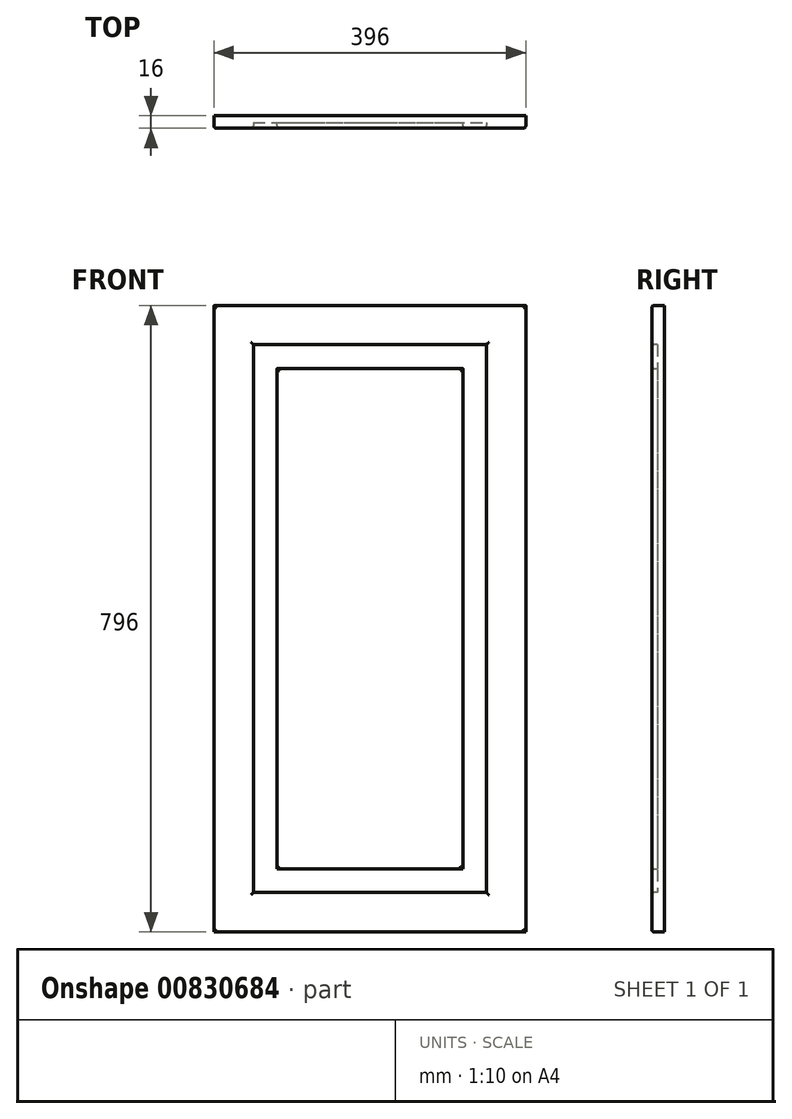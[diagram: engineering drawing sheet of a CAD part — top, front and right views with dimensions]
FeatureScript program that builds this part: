
annotation { "Feature Type Name" : "Feature", "Feature Type Description" : "" }
export const myFeature = defineFeature(function(context is Context, id is Id, definition is map)
    precondition{}
    {
        {
            var Q0;
            Q0=qCreatedBy(makeId("Front.planeOp"),FACE);
            var sketch = newSketch(context, id + "F0", { "sketchPlane" : qUnion([Q0])});
            skLineSegment(sketch, "E0.bottom", {"start": v(0, 0) * mm, "end": v(44.66, 0) * mm});
            skLineSegment(sketch, "E0.top", {"start": v(0, 33.8) * mm, "end": v(44.66, 33.8) * mm});
            skLineSegment(sketch, "E0.left", {"start": v(0, 0) * mm, "end": v(0, 33.8) * mm});
            skLineSegment(sketch, "E0.right", {"start": v(44.66, 0) * mm, "end": v(44.66, 33.8) * mm});
            skSolve(sketch);
        }
        {
            var Q0;
            Q0=makeQuery(id+"F0.imprint","IMPRINT",FACE,{"disambiguationData":[TD([[makeQuery(id+"F0.imprint","IMPRINT",EDGE,{"derivedFrom":sQuery(id+"F0.wireOp",EDGE,"E0.bottom")}),1.0]])]});
            extrude(context, id + "F1", {"entities" : qUnion([Q0]), "depth" : 16 * mm, "offsetDistance" : 25.4 * mm});
        }
        {
            var Q0;
            Q0=makeQuery(id+"F1.opExtrude","SWEPT_FACE",FACE,{"disambiguationData":[OSD([sQuery(id+"F0.wireOp",EDGE,"E0.bottom")])]});
            extrude(context, id + "F2", {"entities" : qUnion([Q0]), "operationType" : NewBodyOperationType.ADD, "oppositeDirection" : true, "depth" : 796 * mm, "offsetDistance" : 25 * mm});
        }
        {
            var Q0;
            {var subQ0=sQuery(id+"F0.wireOp",EDGE,"E0.left");Q0=makeQuery(id+"F2.boolean.opBoolean","MERGE",FACE,{"derivedFrom":[makeQuery(id+"F1.opExtrude","SWEPT_FACE",FACE,{"disambiguationData":[OSD([subQ0])]}),makeQuery(id+"F2.opExtrude","SWEPT_FACE",FACE,{"disambiguationData":[OSD([sQuery(id+"F0.wireOp",EDGE,"E0.bottom"),subQ0])]})]});}
            extrude(context, id + "F3", {"entities" : qUnion([Q0]), "operationType" : NewBodyOperationType.ADD, "oppositeDirection" : true, "depth" : 196 * mm, "offsetDistance" : 25 * mm});
        }
        {
            var Q0;
            {var subQ0=sQuery(id+"F0.wireOp",EDGE,"E0.left");var subQ1=sQuery(id+"F0.wireOp",EDGE,"E0.bottom");Q0=makeQuery(id+"F3.boolean.opBoolean","MERGE",FACE,{"derivedFrom":[makeQuery(id+"F2.boolean.opBoolean","MERGE",FACE,{"derivedFrom":[makeQuery(id+"F1.opExtrude","CAP_FACE",FACE,{"disambiguationData":[OSD([subQ1,sQuery(id+"F0.wireOp",EDGE,"E0.top"),subQ0,sQuery(id+"F0.wireOp",EDGE,"E0.right")])],"isStart":false}),makeQuery(id+"F2.opExtrude","SWEPT_FACE",FACE,{"disambiguationData":[OSD([subQ1]),TDD([makeQuery(id+"F1.opExtrude","CAP_EDGE",EDGE,{"disambiguationData":[OSD([subQ1])],"isStart":false})])]})]}),makeQuery(id+"F3.opExtrude","SWEPT_FACE",FACE,{"disambiguationData":[OSD([subQ1,subQ0]),TDD([makeQuery(id+"F2.boolean.opBoolean","MERGE",EDGE,{"derivedFrom":[makeQuery(id+"F1.opExtrude","CAP_EDGE",EDGE,{"disambiguationData":[OSD([subQ0])],"isStart":false}),makeQuery(id+"F2.opExtrude","SWEPT_EDGE",EDGE,{"disambiguationData":[OSD([subQ1,subQ0]),TDD([makeQuery(id+"F1.opExtrude","CAP_VERTEX",VERTEX,{"disambiguationData":[OSD([subQ1,subQ0])],"isStart":false})])]})]})])]})]});}
            var sketch = newSketch(context, id + "F4", { "sketchPlane" : qUnion([Q0])});
            skLineSegment(sketch, "E1.bottom", {"start": v(59.7, 646.67) * mm, "end": v(128.66, 646.67) * mm});
            skLineSegment(sketch, "E1.top", {"start": v(59.7, 152.97) * mm, "end": v(128.66, 152.97) * mm});
            skLineSegment(sketch, "E1.left", {"start": v(59.7, 646.67) * mm, "end": v(59.7, 152.97) * mm});
            skLineSegment(sketch, "E1.right", {"start": v(128.66, 646.67) * mm, "end": v(128.66, 152.97) * mm});
            skSolve(sketch);
        }
        {
            var Q0;
            Q0=makeQuery(id+"F4.imprint","IMPRINT",FACE,{"disambiguationData":[TD([[makeQuery(id+"F4.imprint","IMPRINT",EDGE,{"derivedFrom":sQuery(id+"F4.wireOp",EDGE,"E1.bottom")}),-1.0]])]});
            extrude(context, id + "F5", {"entities" : qUnion([Q0]), "operationType" : NewBodyOperationType.REMOVE, "oppositeDirection" : true, "depth" : 7 * mm, "offsetDistance" : 25 * mm});
        }
        {
            var Q0;
            Q0=makeQuery(id+"F5.boolean.opBoolean","COPY",FACE,{"derivedFrom":makeQuery(id+"F5.opExtrude","SWEPT_FACE",FACE,{"disambiguationData":[OSD([sQuery(id+"F4.wireOp",EDGE,"E1.left")])]})});
            extrude(context, id + "F6", {"entities" : qUnion([Q0]), "operationType" : NewBodyOperationType.REMOVE, "oppositeDirection" : true, "depth" : 9.7 * mm, "offsetDistance" : 25 * mm});
        }
        {
            var Q0;
            {var subQ0=sQuery(id+"F4.wireOp",EDGE,"E1.bottom");Q0=makeQuery(id+"F6.boolean.opBoolean","MERGE",FACE,{"derivedFrom":[makeQuery(id+"F5.boolean.opBoolean","COPY",FACE,{"derivedFrom":makeQuery(id+"F5.opExtrude","SWEPT_FACE",FACE,{"disambiguationData":[OSD([subQ0])]})}),makeQuery(id+"F6.opExtrude","SWEPT_FACE",FACE,{"disambiguationData":[OSD([subQ0,sQuery(id+"F4.wireOp",EDGE,"E1.left")])]})]});}
            extrude(context, id + "F7", {"entities" : qUnion([Q0]), "operationType" : NewBodyOperationType.ADD, "oppositeDirection" : true, "depth" : 99.33 * mm, "offsetDistance" : 25 * mm});
        }
        {
            var Q0;
            {var subQ0=sQuery(id+"F4.wireOp",EDGE,"E1.bottom");Q0=makeQuery(id+"F6.boolean.opBoolean","MERGE",FACE,{"derivedFrom":[makeQuery(id+"F5.boolean.opBoolean","COPY",FACE,{"derivedFrom":makeQuery(id+"F5.opExtrude","SWEPT_FACE",FACE,{"disambiguationData":[OSD([subQ0])]})}),makeQuery(id+"F6.opExtrude","SWEPT_FACE",FACE,{"disambiguationData":[OSD([subQ0,sQuery(id+"F4.wireOp",EDGE,"E1.left")])]})]});}
            extrude(context, id + "F8", {"entities" : qUnion([Q0]), "operationType" : NewBodyOperationType.REMOVE, "oppositeDirection" : true, "depth" : 99.33 * mm, "offsetDistance" : 25 * mm});
        }
        {
            var Q0;
            {var subQ0=sQuery(id+"F4.wireOp",EDGE,"E1.right");Q0=makeQuery(id+"F8.boolean.opBoolean","MERGE",FACE,{"derivedFrom":[makeQuery(id+"F5.boolean.opBoolean","COPY",FACE,{"derivedFrom":makeQuery(id+"F5.opExtrude","SWEPT_FACE",FACE,{"disambiguationData":[OSD([subQ0])]})}),makeQuery(id+"F8.opExtrude","SWEPT_FACE",FACE,{"disambiguationData":[OSD([sQuery(id+"F4.wireOp",EDGE,"E1.bottom"),subQ0])]})]});}
            extrude(context, id + "F9", {"entities" : qUnion([Q0]), "operationType" : NewBodyOperationType.REMOVE, "oppositeDirection" : true, "depth" : 17.34 * mm, "offsetDistance" : 25 * mm});
        }
        {
            var Q0;
            {var subQ0=sQuery(id+"F4.wireOp",EDGE,"E1.top");Q0=makeQuery(id+"F9.boolean.opBoolean","MERGE",FACE,{"derivedFrom":[makeQuery(id+"F6.boolean.opBoolean","MERGE",FACE,{"derivedFrom":[makeQuery(id+"F5.boolean.opBoolean","COPY",FACE,{"derivedFrom":makeQuery(id+"F5.opExtrude","SWEPT_FACE",FACE,{"disambiguationData":[OSD([subQ0])]})}),makeQuery(id+"F6.opExtrude","SWEPT_FACE",FACE,{"disambiguationData":[OSD([subQ0,sQuery(id+"F4.wireOp",EDGE,"E1.left")])]})]}),makeQuery(id+"F9.opExtrude","SWEPT_FACE",FACE,{"disambiguationData":[OSD([subQ0,sQuery(id+"F4.wireOp",EDGE,"E1.right")])]})]});}
            extrude(context, id + "F10", {"entities" : qUnion([Q0]), "operationType" : NewBodyOperationType.REMOVE, "oppositeDirection" : true, "depth" : 102.97 * mm, "offsetDistance" : 25 * mm});
        }
        {
            var Q0;
            {var subQ0=sQuery(id+"F4.wireOp",EDGE,"E1.right");var subQ1=sQuery(id+"F4.wireOp",EDGE,"E1.top");var subQ2=sQuery(id+"F4.wireOp",EDGE,"E1.left");var subQ3=sQuery(id+"F4.wireOp",EDGE,"E1.bottom");Q0=makeQuery(id+"F10.boolean.opBoolean","MERGE",FACE,{"derivedFrom":[makeQuery(id+"F9.boolean.opBoolean","MERGE",FACE,{"derivedFrom":[makeQuery(id+"F8.boolean.opBoolean","MERGE",FACE,{"derivedFrom":[makeQuery(id+"F6.boolean.opBoolean","MERGE",FACE,{"derivedFrom":[makeQuery(id+"F5.boolean.opBoolean","COPY",FACE,{"derivedFrom":makeQuery(id+"F5.opExtrude","CAP_FACE",FACE,{"disambiguationData":[OSD([subQ3,subQ1,subQ2,subQ0])],"isStart":false})}),makeQuery(id+"F6.opExtrude","SWEPT_FACE",FACE,{"disambiguationData":[OSD([subQ2]),TDD([makeQuery(id+"F5.boolean.opBoolean","COPY",EDGE,{"derivedFrom":makeQuery(id+"F5.opExtrude","CAP_EDGE",EDGE,{"disambiguationData":[OSD([subQ2])],"isStart":false})})])]})]}),makeQuery(id+"F8.opExtrude","SWEPT_FACE",FACE,{"disambiguationData":[OSD([subQ3,subQ2]),TDD([makeQuery(id+"F6.boolean.opBoolean","MERGE",EDGE,{"derivedFrom":[makeQuery(id+"F5.boolean.opBoolean","COPY",EDGE,{"derivedFrom":makeQuery(id+"F5.opExtrude","CAP_EDGE",EDGE,{"disambiguationData":[OSD([subQ3])],"isStart":false})}),makeQuery(id+"F6.opExtrude","SWEPT_EDGE",EDGE,{"disambiguationData":[OSD([subQ3,subQ2]),TDD([makeQuery(id+"F5.boolean.opBoolean","COPY",VERTEX,{"derivedFrom":makeQuery(id+"F5.opExtrude","CAP_VERTEX",VERTEX,{"disambiguationData":[OSD([subQ3,subQ2])],"isStart":false})})])]})]})])]})]}),makeQuery(id+"F9.opExtrude","SWEPT_FACE",FACE,{"disambiguationData":[OSD([subQ3,subQ0]),TDD([makeQuery(id+"F8.boolean.opBoolean","MERGE",EDGE,{"derivedFrom":[makeQuery(id+"F5.boolean.opBoolean","COPY",EDGE,{"derivedFrom":makeQuery(id+"F5.opExtrude","CAP_EDGE",EDGE,{"disambiguationData":[OSD([subQ0])],"isStart":false})}),makeQuery(id+"F8.opExtrude","SWEPT_EDGE",EDGE,{"disambiguationData":[OSD([subQ3,subQ0]),TDD([makeQuery(id+"F5.boolean.opBoolean","COPY",VERTEX,{"derivedFrom":makeQuery(id+"F5.opExtrude","CAP_VERTEX",VERTEX,{"disambiguationData":[OSD([subQ3,subQ0])],"isStart":false})})])]})]})])]})]}),makeQuery(id+"F10.opExtrude","SWEPT_FACE",FACE,{"disambiguationData":[OSD([subQ1,subQ2,subQ0]),TDD([makeQuery(id+"F9.boolean.opBoolean","MERGE",EDGE,{"derivedFrom":[makeQuery(id+"F6.boolean.opBoolean","MERGE",EDGE,{"derivedFrom":[makeQuery(id+"F5.boolean.opBoolean","COPY",EDGE,{"derivedFrom":makeQuery(id+"F5.opExtrude","CAP_EDGE",EDGE,{"disambiguationData":[OSD([subQ1])],"isStart":false})}),makeQuery(id+"F6.opExtrude","SWEPT_EDGE",EDGE,{"disambiguationData":[OSD([subQ1,subQ2]),TDD([makeQuery(id+"F5.boolean.opBoolean","COPY",VERTEX,{"derivedFrom":makeQuery(id+"F5.opExtrude","CAP_VERTEX",VERTEX,{"disambiguationData":[OSD([subQ1,subQ2])],"isStart":false})})])]})]}),makeQuery(id+"F9.opExtrude","SWEPT_EDGE",EDGE,{"disambiguationData":[OSD([subQ1,subQ0]),TDD([makeQuery(id+"F5.boolean.opBoolean","COPY",VERTEX,{"derivedFrom":makeQuery(id+"F5.opExtrude","CAP_VERTEX",VERTEX,{"disambiguationData":[OSD([subQ1,subQ0])],"isStart":false})})])]})]})])]})]});}
            var sketch = newSketch(context, id + "F11", { "sketchPlane" : qUnion([Q0])});
            skLineSegment(sketch, "E2.bottom", {"start": v(74.13, 678.73) * mm, "end": v(109.41, 678.73) * mm});
            skLineSegment(sketch, "E2.top", {"start": v(74.13, 186.63) * mm, "end": v(109.41, 186.63) * mm});
            skLineSegment(sketch, "E2.left", {"start": v(74.13, 678.73) * mm, "end": v(74.13, 186.63) * mm});
            skLineSegment(sketch, "E2.right", {"start": v(109.41, 678.73) * mm, "end": v(109.41, 186.63) * mm});
            skSolve(sketch);
        }
        {
            var Q0;
            Q0=makeQuery(id+"F11.imprint","IMPRINT",FACE,{"disambiguationData":[TD([[makeQuery(id+"F11.imprint","IMPRINT",EDGE,{"derivedFrom":sQuery(id+"F11.wireOp",EDGE,"E2.bottom")}),-1.0]])]});
            extrude(context, id + "F12", {"entities" : qUnion([Q0]), "operationType" : NewBodyOperationType.ADD, "depth" : 7 * mm, "offsetDistance" : 25 * mm});
        }
        {
            var Q0;
            Q0=makeQuery(id+"F12.opExtrude","SWEPT_FACE",FACE,{"disambiguationData":[OSD([sQuery(id+"F11.wireOp",EDGE,"E2.bottom")])]});
            extrude(context, id + "F13", {"entities" : qUnion([Q0]), "operationType" : NewBodyOperationType.ADD, "depth" : 37.27 * mm, "offsetDistance" : 25 * mm});
        }
        {
            var Q0;
            {var subQ0=sQuery(id+"F11.wireOp",EDGE,"E2.right");Q0=makeQuery(id+"F13.boolean.opBoolean","MERGE",FACE,{"derivedFrom":[makeQuery(id+"F12.opExtrude","SWEPT_FACE",FACE,{"disambiguationData":[OSD([subQ0])]}),makeQuery(id+"F13.opExtrude","SWEPT_FACE",FACE,{"disambiguationData":[OSD([sQuery(id+"F11.wireOp",EDGE,"E2.bottom"),subQ0])]})]});}
            extrude(context, id + "F14", {"entities" : qUnion([Q0]), "operationType" : NewBodyOperationType.ADD, "depth" : 6.58 * mm, "offsetDistance" : 25 * mm});
        }
        {
            var Q0;
            {var subQ0=sQuery(id+"F11.wireOp",EDGE,"E2.top");Q0=makeQuery(id+"F14.boolean.opBoolean","MERGE",FACE,{"derivedFrom":[makeQuery(id+"F12.opExtrude","SWEPT_FACE",FACE,{"disambiguationData":[OSD([subQ0])]}),makeQuery(id+"F14.opExtrude","SWEPT_FACE",FACE,{"disambiguationData":[OSD([subQ0,sQuery(id+"F11.wireOp",EDGE,"E2.right")])]})]});}
            extrude(context, id + "F15", {"entities" : qUnion([Q0]), "operationType" : NewBodyOperationType.ADD, "depth" : 106.63 * mm, "offsetDistance" : 25 * mm});
        }
        {
            var Q0;
            {var subQ0=sQuery(id+"F11.wireOp",EDGE,"E2.left");Q0=makeQuery(id+"F15.boolean.opBoolean","MERGE",FACE,{"derivedFrom":[makeQuery(id+"F13.boolean.opBoolean","MERGE",FACE,{"derivedFrom":[makeQuery(id+"F12.opExtrude","SWEPT_FACE",FACE,{"disambiguationData":[OSD([subQ0])]}),makeQuery(id+"F13.opExtrude","SWEPT_FACE",FACE,{"disambiguationData":[OSD([sQuery(id+"F11.wireOp",EDGE,"E2.bottom"),subQ0])]})]}),makeQuery(id+"F15.opExtrude","SWEPT_FACE",FACE,{"disambiguationData":[OSD([sQuery(id+"F11.wireOp",EDGE,"E2.top"),subQ0])]})]});}
            extrude(context, id + "F16", {"entities" : qUnion([Q0]), "operationType" : NewBodyOperationType.REMOVE, "oppositeDirection" : true, "depth" : 5.87 * mm, "offsetDistance" : 25 * mm});
        }
        {
            var Q0;
            Q0=makeQuery(id+"F3.opExtrude","CAP_FACE",FACE,{"disambiguationData":[OSD([sQuery(id+"F0.wireOp",EDGE,"E0.bottom"),sQuery(id+"F0.wireOp",EDGE,"E0.left")])],"isStart":false});
            extrude(context, id + "F17", {"entities" : qUnion([Q0]), "operationType" : NewBodyOperationType.ADD, "depth" : 200 * mm, "offsetDistance" : 25 * mm});
        }
        {
            var Q0;
            {var subQ0=sQuery(id+"F4.wireOp",EDGE,"E1.right");Q0=makeQuery(id+"F10.boolean.opBoolean","MERGE",FACE,{"derivedFrom":[makeQuery(id+"F9.boolean.opBoolean","COPY",FACE,{"derivedFrom":makeQuery(id+"F9.opExtrude","CAP_FACE",FACE,{"disambiguationData":[OSD([sQuery(id+"F4.wireOp",EDGE,"E1.bottom"),subQ0])],"isStart":false})}),makeQuery(id+"F10.opExtrude","SWEPT_FACE",FACE,{"disambiguationData":[OSD([sQuery(id+"F4.wireOp",EDGE,"E1.top"),subQ0])]})]});}
            extrude(context, id + "F18", {"entities" : qUnion([Q0]), "operationType" : NewBodyOperationType.REMOVE, "oppositeDirection" : true, "depth" : 200 * mm, "offsetDistance" : 25 * mm});
        }
        {
            var Q0;
            {var subQ0=sQuery(id+"F11.wireOp",EDGE,"E2.right");var subQ1=sQuery(id+"F11.wireOp",EDGE,"E2.top");Q0=makeQuery(id+"F15.boolean.opBoolean","MERGE",FACE,{"derivedFrom":[makeQuery(id+"F14.opExtrude","CAP_FACE",FACE,{"disambiguationData":[OSD([sQuery(id+"F11.wireOp",EDGE,"E2.bottom"),subQ0])],"isStart":false}),makeQuery(id+"F15.opExtrude","SWEPT_FACE",FACE,{"disambiguationData":[OSD([subQ1,subQ0]),TDD([makeQuery(id+"F14.opExtrude","CAP_EDGE",EDGE,{"disambiguationData":[OSD([subQ1,subQ0])],"isStart":false})])]})]});}
            extrude(context, id + "F19", {"entities" : qUnion([Q0]), "operationType" : NewBodyOperationType.ADD, "depth" : 200 * mm, "offsetDistance" : 25 * mm});
        }
        {
            var Q0;
            {var subQ0=sQuery(id+"F11.wireOp",EDGE,"E2.right");var subQ1=sQuery(id+"F11.wireOp",EDGE,"E2.top");var subQ2=makeQuery(id+"F12.opExtrude","CAP_VERTEX",VERTEX,{"disambiguationData":[OSD([subQ1,subQ0])],"isStart":false});var subQ3=sQuery(id+"F11.wireOp",EDGE,"E2.bottom");var subQ4=makeQuery(id+"F13.boolean.opBoolean","MERGE",EDGE,{"derivedFrom":[makeQuery(id+"F12.opExtrude","CAP_EDGE",EDGE,{"disambiguationData":[OSD([subQ0])],"isStart":false}),makeQuery(id+"F13.opExtrude","SWEPT_EDGE",EDGE,{"disambiguationData":[OSD([subQ3,subQ0]),TDD([makeQuery(id+"F12.opExtrude","CAP_VERTEX",VERTEX,{"disambiguationData":[OSD([subQ3,subQ0])],"isStart":false})])]})]});Q0=makeQuery(id+"F19.boolean.opBoolean","MERGE",FACE,{"derivedFrom":[makeQuery(id+"F15.boolean.opBoolean","MERGE",FACE,{"derivedFrom":[makeQuery(id+"F14.boolean.opBoolean","MERGE",FACE,{"derivedFrom":[makeQuery(id+"F13.boolean.opBoolean","MERGE",FACE,{"derivedFrom":[makeQuery(id+"F12.opExtrude","CAP_FACE",FACE,{"disambiguationData":[OSD([subQ3,subQ1,sQuery(id+"F11.wireOp",EDGE,"E2.left"),subQ0])],"isStart":false}),makeQuery(id+"F13.opExtrude","SWEPT_FACE",FACE,{"disambiguationData":[OSD([subQ3]),TDD([makeQuery(id+"F12.opExtrude","CAP_EDGE",EDGE,{"disambiguationData":[OSD([subQ3])],"isStart":false})])]})]}),makeQuery(id+"F14.opExtrude","SWEPT_FACE",FACE,{"disambiguationData":[OSD([subQ3,subQ0]),TDD([subQ4])]})]}),makeQuery(id+"F15.opExtrude","SWEPT_FACE",FACE,{"disambiguationData":[OSD([subQ1,subQ0]),TDD([makeQuery(id+"F14.boolean.opBoolean","MERGE",EDGE,{"derivedFrom":[makeQuery(id+"F12.opExtrude","CAP_EDGE",EDGE,{"disambiguationData":[OSD([subQ1])],"isStart":false}),makeQuery(id+"F14.opExtrude","SWEPT_EDGE",EDGE,{"disambiguationData":[OSD([subQ1,subQ0]),TDD([subQ2])]})]})])]})]}),makeQuery(id+"F19.opExtrude","SWEPT_FACE",FACE,{"disambiguationData":[OSD([subQ3,subQ1,subQ0]),TDD([makeQuery(id+"F15.boolean.opBoolean","MERGE",EDGE,{"derivedFrom":[makeQuery(id+"F14.opExtrude","CAP_EDGE",EDGE,{"disambiguationData":[OSD([subQ3,subQ0]),TDD([subQ4])],"isStart":false}),makeQuery(id+"F15.opExtrude","SWEPT_EDGE",EDGE,{"disambiguationData":[OSD([subQ1,subQ0]),TDD([makeQuery(id+"F14.opExtrude","CAP_VERTEX",VERTEX,{"disambiguationData":[OSD([subQ1,subQ0]),TDD([subQ2])],"isStart":false})])]})]})])]})]});}
            var Q1;
            {var subQ0=sQuery(id+"F0.wireOp",EDGE,"E0.left");var subQ1=sQuery(id+"F0.wireOp",EDGE,"E0.bottom");var subQ2=makeQuery(id+"F2.boolean.opBoolean","MERGE",EDGE,{"derivedFrom":[makeQuery(id+"F1.opExtrude","CAP_EDGE",EDGE,{"disambiguationData":[OSD([subQ0])],"isStart":false}),makeQuery(id+"F2.opExtrude","SWEPT_EDGE",EDGE,{"disambiguationData":[OSD([subQ1,subQ0]),TDD([makeQuery(id+"F1.opExtrude","CAP_VERTEX",VERTEX,{"disambiguationData":[OSD([subQ1,subQ0])],"isStart":false})])]})]});Q1=makeQuery(id+"F17.boolean.opBoolean","MERGE",FACE,{"derivedFrom":[makeQuery(id+"F3.boolean.opBoolean","MERGE",FACE,{"derivedFrom":[makeQuery(id+"F2.boolean.opBoolean","MERGE",FACE,{"derivedFrom":[makeQuery(id+"F1.opExtrude","CAP_FACE",FACE,{"disambiguationData":[OSD([subQ1,sQuery(id+"F0.wireOp",EDGE,"E0.top"),subQ0,sQuery(id+"F0.wireOp",EDGE,"E0.right")])],"isStart":false}),makeQuery(id+"F2.opExtrude","SWEPT_FACE",FACE,{"disambiguationData":[OSD([subQ1]),TDD([makeQuery(id+"F1.opExtrude","CAP_EDGE",EDGE,{"disambiguationData":[OSD([subQ1])],"isStart":false})])]})]}),makeQuery(id+"F3.opExtrude","SWEPT_FACE",FACE,{"disambiguationData":[OSD([subQ1,subQ0]),TDD([subQ2])]})]}),makeQuery(id+"F17.opExtrude","SWEPT_FACE",FACE,{"disambiguationData":[OSD([subQ1,subQ0]),TDD([makeQuery(id+"F3.opExtrude","CAP_EDGE",EDGE,{"disambiguationData":[OSD([subQ1,subQ0]),TDD([subQ2])],"isStart":false})])]})]});}
            fillet(context, id + "F20", {"entities" : qUnion([Q0, Q1]), "radius" : 3 * mm, "tangentPropagation" : true, "allowEdgeOverflow" : false});
        }
    });
